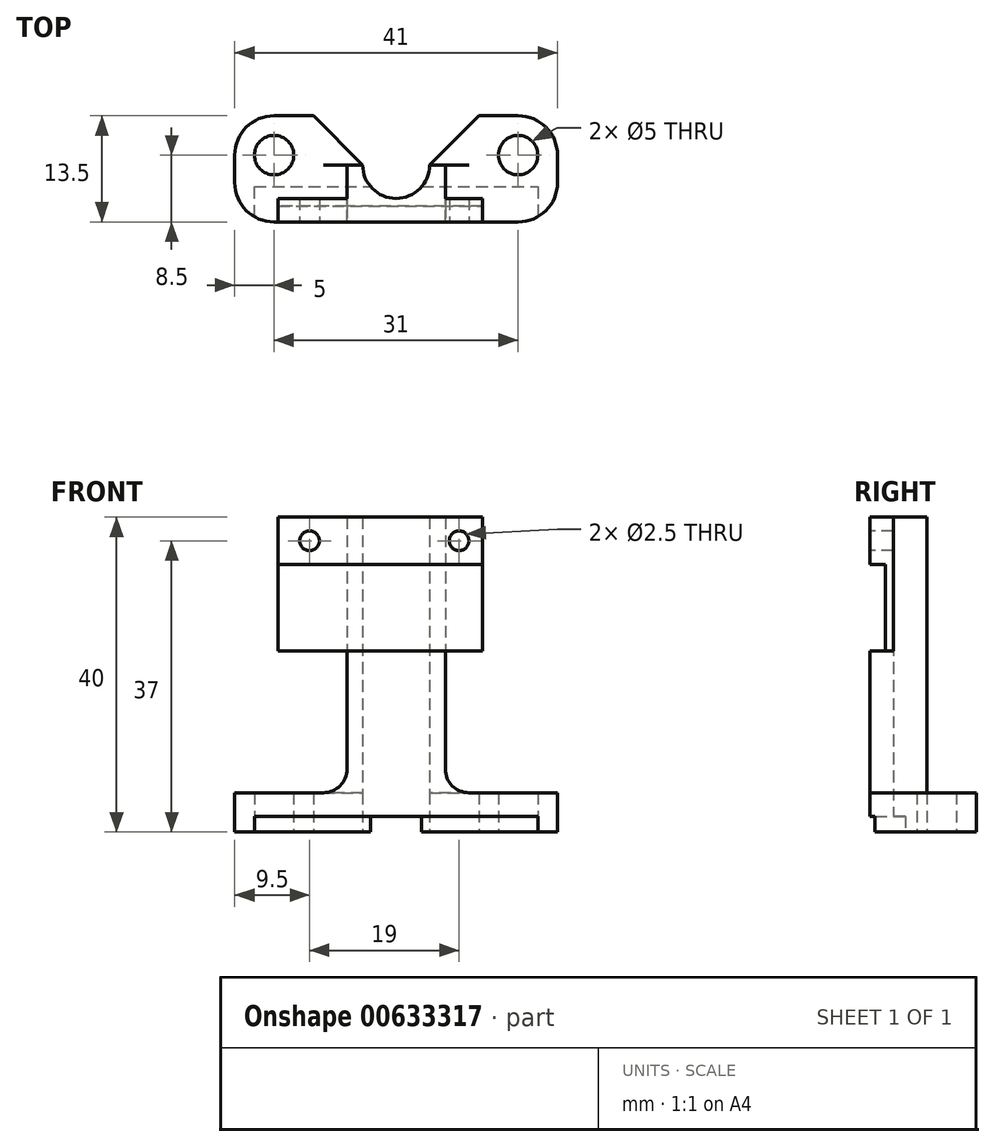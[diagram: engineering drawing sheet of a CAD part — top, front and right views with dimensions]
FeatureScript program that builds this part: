
annotation { "Feature Type Name" : "Feature", "Feature Type Description" : "" }
export const myFeature = defineFeature(function(context is Context, id is Id, definition is map)
    precondition{}
    {
        {
            var Q0;
            Q0=qCreatedBy(makeId("Top.planeOp"),FACE);
            var sketch = newSketch(context, id + "F0", { "sketchPlane" : qUnion([Q0])});
            skCircle(sketch, "E0", {"center": v(-15.5, 0) * mm, "radius": 2.5 * mm});
            skCircle(sketch, "E1", {"center": v(0, -1.25) * mm, "radius": 4.25 * mm});
            skLineSegment(sketch, "E2", {"start": v(0, -1.25) * mm, "end": v(-4.25, -1.25) * mm, "construction": true});
            skLineSegment(sketch, "E3", {"start": v(-4.25, -1.25) * mm, "end": v(-10.5, 5) * mm});
            skLineSegment(sketch, "E4", {"start": v(-10.5, 5) * mm, "end": v(-20.5, 5) * mm});
            skLineSegment(sketch, "E5", {"start": v(-20.5, 5) * mm, "end": v(-20.5, -8.5) * mm});
            skLineSegment(sketch, "E6", {"start": v(-20.5, -8.5) * mm, "end": v(0, -8.5) * mm});
            skLineSegment(sketch, "E7.MirrorCS", {"start": v(4.25, -1.25) * mm, "end": v(10.5, 5) * mm});
            skLineSegment(sketch, "E8.MirrorCS", {"start": v(20.5, -8.5) * mm, "end": v(0, -8.5) * mm});
            skLineSegment(sketch, "E9.MirrorCS", {"start": v(20.5, 5) * mm, "end": v(20.5, -8.5) * mm});
            skLineSegment(sketch, "E10.MirrorCS", {"start": v(10.5, 5) * mm, "end": v(20.5, 5) * mm});
            skCircle(sketch, "E11.MirrorC", {"center": v(15.5, 0) * mm, "radius": 2.5 * mm});
            skPoint(sketch, "E12", {"position": v(0, -5.5) * mm});
            skSolve(sketch);
        }
        {
            var Q0;
            Q0=makeQuery(id+"F0.imprint","IMPRINT",FACE,{"disambiguationData":[TD([[makeQuery(id+"F0.imprint","IMPRINT",EDGE,{"derivedFrom":sQuery(id+"F0.wireOp",EDGE,"E0")}),-1.0]])]});
            extrude(context, id + "F1", {"entities" : qUnion([Q0]), "depth" : 5 * mm, "offsetDistance" : 25 * mm});
        }
        {
            var Q0;
            Q0=makeQuery(id+"F1.opExtrude","CAP_FACE",FACE,{"disambiguationData":[OSD([sQuery(id+"F0.wireOp",EDGE,"E0"),sQuery(id+"F0.wireOp",EDGE,"E1"),sQuery(id+"F0.wireOp",EDGE,"E3"),sQuery(id+"F0.wireOp",EDGE,"E4"),sQuery(id+"F0.wireOp",EDGE,"E5"),sQuery(id+"F0.wireOp",EDGE,"E6"),sQuery(id+"F0.wireOp",EDGE,"E7.MirrorCS"),sQuery(id+"F0.wireOp",EDGE,"E8.MirrorCS"),sQuery(id+"F0.wireOp",EDGE,"E9.MirrorCS"),sQuery(id+"F0.wireOp",EDGE,"E10.MirrorCS"),sQuery(id+"F0.wireOp",EDGE,"E11.MirrorC")])],"isStart":true});
            var sketch = newSketch(context, id + "F2", { "sketchPlane" : qUnion([Q0])});
            skLineSegment(sketch, "E13", {"start": v(-4.25, 1.25) * mm, "end": v(-6.25, 1.25) * mm});
            skLineSegment(sketch, "E14", {"start": v(-6.25, 1.25) * mm, "end": v(-6.25, 8.5) * mm});
            skLineSegment(sketch, "E15.MirrorCS", {"start": v(6.25, 1.25) * mm, "end": v(6.25, 8.5) * mm});
            skLineSegment(sketch, "E16.MirrorCS", {"start": v(4.25, 1.25) * mm, "end": v(6.25, 1.25) * mm});
            skSolve(sketch);
        }
        {
            var Q0;
            Q0=makeQuery(id+"F2.imprint","IMPRINT",FACE,{"disambiguationData":[TD([[makeQuery(id+"F2.imprint","IMPRINT",EDGE,{"derivedFrom":sQuery(id+"F2.wireOp",EDGE,"E13")}),-1.0]])]});
            extrude(context, id + "F3", {"entities" : qUnion([Q0]), "operationType" : NewBodyOperationType.ADD, "oppositeDirection" : true, "depth" : 40 * mm, "offsetDistance" : 25 * mm});
        }
        {
            var Q0;
            Q0=makeQuery(id+"F3.opExtrude","CAP_FACE",FACE,{"disambiguationData":[OSD([sQuery(id+"F0.wireOp",EDGE,"E1"),sQuery(id+"F0.wireOp",EDGE,"E6"),sQuery(id+"F0.wireOp",EDGE,"E8.MirrorCS"),sQuery(id+"F2.wireOp",EDGE,"E13"),sQuery(id+"F2.wireOp",EDGE,"E14"),sQuery(id+"F2.wireOp",EDGE,"E15.MirrorCS"),sQuery(id+"F2.wireOp",EDGE,"E16.MirrorCS")])],"isStart":false});
            var sketch = newSketch(context, id + "F4", { "sketchPlane" : qUnion([Q0])});
            skLineSegment(sketch, "E17", {"start": v(-15, -5.5) * mm, "end": v(0, -5.5) * mm});
            skPoint(sketch, "E17.startSnap0", {"position": v(0, -5.5) * mm});
            skLineSegment(sketch, "E18", {"start": v(0, -5.5) * mm, "end": v(11, -5.5) * mm});
            skLineSegment(sketch, "E19", {"start": v(11, -5.5) * mm, "end": v(11, -8.5) * mm});
            skLineSegment(sketch, "E20", {"start": v(11, -8.5) * mm, "end": v(-15, -8.5) * mm});
            skLineSegment(sketch, "E21", {"start": v(-15, -8.5) * mm, "end": v(-15, -5.5) * mm});
            skSolve(sketch);
        }
        {
            var Q0;
            {var subQ0=sQuery(id+"F4.wireOp",EDGE,"E21");Q0=makeQuery(id+"F4.imprint","IMPRINT",FACE,{"disambiguationData":[TD([[makeQuery(id+"F4.imprint","IMPRINT",EDGE,{"derivedFrom":subQ0}),-1.0]])]});}
            var Q1;
            {var subQ0=sQuery(id+"F4.wireOp",EDGE,"E20");var subQ1=makeQuery(id+"F3.opExtrude","CAP_EDGE",EDGE,{"disambiguationData":[OSD([sQuery(id+"F2.wireOp",EDGE,"E14")])],"isStart":false});var subQ2=makeQuery(id+"F4.imprint","INTERSECT",VERTEX,{"derivedFrom":[subQ1,subQ0]});var subQ7=makeQuery(id+"F3.opExtrude","CAP_EDGE",EDGE,{"disambiguationData":[OSD([sQuery(id+"F2.wireOp",EDGE,"E15.MirrorCS")])],"isStart":false});var subQ9=makeQuery(id+"F4.imprint","INTERSECT",VERTEX,{"derivedFrom":[subQ7,subQ0]});Q1=makeQuery(id+"F4.imprint","IMPRINT",FACE,{"disambiguationData":[TD([[makeQuery(id+"F4.imprint","IMPRINT",EDGE,{"disambiguationData":[TD([[subQ2,-1.0],[subQ9,1.0]])],"derivedFrom":subQ0}),1.0]])]});}
            var Q2;
            {var subQ0=sQuery(id+"F4.wireOp",EDGE,"E19");Q2=makeQuery(id+"F4.imprint","IMPRINT",FACE,{"disambiguationData":[TD([[makeQuery(id+"F4.imprint","IMPRINT",EDGE,{"derivedFrom":subQ0}),-1.0]])]});}
            extrude(context, id + "F5", {"entities" : qUnion([Q0, Q1, Q2]), "operationType" : NewBodyOperationType.ADD, "oppositeDirection" : true, "depth" : 17 * mm, "offsetDistance" : 25 * mm});
        }
        {
            var Q0;
            {var subQ0=sQuery(id+"F0.wireOp",EDGE,"E8.MirrorCS");var subQ1=sQuery(id+"F0.wireOp",EDGE,"E6");Q0=makeQuery(id+"F5.boolean.opBoolean","MERGE",FACE,{"derivedFrom":[makeQuery(id+"F3.boolean.opBoolean","MERGE",FACE,{"derivedFrom":[makeQuery(id+"F1.opExtrude","SWEPT_FACE",FACE,{"disambiguationData":[OSD([subQ1,subQ0])]}),makeQuery(id+"F3.opExtrude","SWEPT_FACE",FACE,{"disambiguationData":[OSD([subQ1,subQ0])]})]}),makeQuery(id+"F5.opExtrude","SWEPT_FACE",FACE,{"disambiguationData":[OSD([sQuery(id+"F4.wireOp",EDGE,"E20")])]})]});}
            var sketch = newSketch(context, id + "F6", { "sketchPlane" : qUnion([Q0])});
            skPoint(sketch, "E22", {"position": v(-11, 37) * mm});
            skPoint(sketch, "E23", {"position": v(8, 37) * mm});
            skLineSegment(sketch, "E24", {"start": v(-15, 34) * mm, "end": v(11, 34) * mm});
            skLineSegment(sketch, "E25", {"start": v(-6.25, 23) * mm, "end": v(6.25, 23) * mm});
            skSolve(sketch);
        }
        {
            var Q0;
            {var subQ11=sQuery(id+"F6.wireOp",EDGE,"E24");Q0=makeQuery(id+"F6.imprint","IMPRINT",FACE,{"disambiguationData":[TD([[makeQuery(id+"F6.imprint","IMPRINT",EDGE,{"derivedFrom":subQ11}),-1.0]])]});}
            extrude(context, id + "F7", {"entities" : qUnion([Q0]), "operationType" : NewBodyOperationType.REMOVE, "oppositeDirection" : true, "depth" : 2 * mm, "offsetDistance" : 25 * mm});
        }
        {
            var Q0;
            Q0=sQuery(id+"F6.wireOp",VERTEX,"E22");
            var Q1;
            Q1=sQuery(id+"F6.wireOp",VERTEX,"E23");
            var Q2;
            Q2=makeQuery(id+"F1.opExtrude","SWEPT_BODY",BODY,{"disambiguationData":[OSD([sQuery(id+"F0.wireOp",EDGE,"E0"),sQuery(id+"F0.wireOp",EDGE,"E1"),sQuery(id+"F0.wireOp",EDGE,"E3"),sQuery(id+"F0.wireOp",EDGE,"E4"),sQuery(id+"F0.wireOp",EDGE,"E5"),sQuery(id+"F0.wireOp",EDGE,"E6"),sQuery(id+"F0.wireOp",EDGE,"E7.MirrorCS"),sQuery(id+"F0.wireOp",EDGE,"E8.MirrorCS"),sQuery(id+"F0.wireOp",EDGE,"E9.MirrorCS"),sQuery(id+"F0.wireOp",EDGE,"E10.MirrorCS"),sQuery(id+"F0.wireOp",EDGE,"E11.MirrorC")])]});
            hole(context, id + "F8", {"style" : HoleStyle.SIMPLE, "endStyle" : HoleEndStyle.THROUGH, "holeDiameter" : 2.5 * mm, "majorDiameter" : 5 * mm, "tappedDepth" : 12 * mm, "tapClearance" : 3, "locations" : qUnion([Q0, Q1]), "scope" : qUnion([Q2])});
        }
        {
            var Q0;
            Q0=makeQuery(id+"F1.opExtrude","SWEPT_EDGE",EDGE,{"disambiguationData":[OSD([sQuery(id+"F0.wireOp",EDGE,"E8.MirrorCS"),sQuery(id+"F0.wireOp",EDGE,"E9.MirrorCS")])]});
            var Q1;
            Q1=makeQuery(id+"F1.opExtrude","SWEPT_EDGE",EDGE,{"disambiguationData":[OSD([sQuery(id+"F0.wireOp",EDGE,"E4"),sQuery(id+"F0.wireOp",EDGE,"E5")])]});
            var Q2;
            Q2=makeQuery(id+"F1.opExtrude","SWEPT_EDGE",EDGE,{"disambiguationData":[OSD([sQuery(id+"F0.wireOp",EDGE,"E5"),sQuery(id+"F0.wireOp",EDGE,"E6")])]});
            var Q3;
            Q3=makeQuery(id+"F1.opExtrude","SWEPT_EDGE",EDGE,{"disambiguationData":[OSD([sQuery(id+"F0.wireOp",EDGE,"E9.MirrorCS"),sQuery(id+"F0.wireOp",EDGE,"E10.MirrorCS")])]});
            fillet(context, id + "F9", {"entities" : qUnion([Q0, Q1, Q2, Q3]), "radius" : 5 * mm, "tangentPropagation" : true, "allowEdgeOverflow" : false});
        }
        {
            var Q0;
            Q0=makeQuery(id+"F1.opExtrude","CAP_FACE",FACE,{"disambiguationData":[OSD([sQuery(id+"F0.wireOp",EDGE,"E0"),sQuery(id+"F0.wireOp",EDGE,"E1"),sQuery(id+"F0.wireOp",EDGE,"E3"),sQuery(id+"F0.wireOp",EDGE,"E4"),sQuery(id+"F0.wireOp",EDGE,"E5"),sQuery(id+"F0.wireOp",EDGE,"E6"),sQuery(id+"F0.wireOp",EDGE,"E7.MirrorCS"),sQuery(id+"F0.wireOp",EDGE,"E8.MirrorCS"),sQuery(id+"F0.wireOp",EDGE,"E9.MirrorCS"),sQuery(id+"F0.wireOp",EDGE,"E10.MirrorCS"),sQuery(id+"F0.wireOp",EDGE,"E11.MirrorC")])],"isStart":true});
            var sketch = newSketch(context, id + "F10", { "sketchPlane" : qUnion([Q0])});
            skPoint(sketch, "E26", {"position": v(-18, 0) * mm});
            skPoint(sketch, "E27", {"position": v(18, 0) * mm});
            skPoint(sketch, "E28", {"position": v(15.5, 0) * mm});
            skPoint(sketch, "E29", {"position": v(-15.5, 0) * mm});
            skPoint(sketch, "E30", {"position": v(-15.5, 2.5) * mm});
            skPoint(sketch, "E31", {"position": v(15.5, 2.5) * mm});
            skLineSegment(sketch, "E32", {"start": v(-18, 7.83) * mm, "end": v(-18, 4) * mm});
            skLineSegment(sketch, "E33", {"start": v(-18, 4) * mm, "end": v(-3.24, 4) * mm});
            skLineSegment(sketch, "E34", {"start": v(18, 4) * mm, "end": v(18, 7.83) * mm});
            skArc(sketch, "E35.0", {"start": v(-3.24, 4) * mm, "mid": v(0, 5.5) * mm, "end": v(3.24, 4) * mm});
            skLineSegment(sketch, "E36.trimOffspring", {"start": v(3.24, 4) * mm, "end": v(18, 4) * mm});
            skPoint(sketch, "E37.orphan", {"position": v(-4.25, 1.25) * mm});
            skPoint(sketch, "E38.orphan", {"position": v(4.25, 1.25) * mm});
            skSolve(sketch);
        }
        {
            var Q0;
            {var subQ4=sQuery(id+"F10.wireOp",EDGE,"E32");Q0=makeQuery(id+"F10.imprint","IMPRINT",FACE,{"disambiguationData":[TD([[makeQuery(id+"F10.imprint","IMPRINT",EDGE,{"derivedFrom":subQ4}),1.0]])]});}
            extrude(context, id + "F11", {"entities" : qUnion([Q0]), "operationType" : NewBodyOperationType.REMOVE, "oppositeDirection" : true, "depth" : 2 * mm, "offsetDistance" : 25 * mm});
        }
        {
            var Q0;
            Q0=makeQuery(id+"F3.boolean.opBoolean","INTERSECT",EDGE,{"derivedFrom":[makeQuery(id+"F1.opExtrude","CAP_FACE",FACE,{"disambiguationData":[OSD([sQuery(id+"F0.wireOp",EDGE,"E0"),sQuery(id+"F0.wireOp",EDGE,"E1"),sQuery(id+"F0.wireOp",EDGE,"E3"),sQuery(id+"F0.wireOp",EDGE,"E4"),sQuery(id+"F0.wireOp",EDGE,"E5"),sQuery(id+"F0.wireOp",EDGE,"E6"),sQuery(id+"F0.wireOp",EDGE,"E7.MirrorCS"),sQuery(id+"F0.wireOp",EDGE,"E8.MirrorCS"),sQuery(id+"F0.wireOp",EDGE,"E9.MirrorCS"),sQuery(id+"F0.wireOp",EDGE,"E10.MirrorCS"),sQuery(id+"F0.wireOp",EDGE,"E11.MirrorC")])],"isStart":false}),makeQuery(id+"F3.opExtrude","SWEPT_FACE",FACE,{"disambiguationData":[OSD([sQuery(id+"F2.wireOp",EDGE,"E15.MirrorCS")])]})]});
            var Q1;
            Q1=makeQuery(id+"F3.boolean.opBoolean","INTERSECT",EDGE,{"derivedFrom":[makeQuery(id+"F1.opExtrude","CAP_FACE",FACE,{"disambiguationData":[OSD([sQuery(id+"F0.wireOp",EDGE,"E0"),sQuery(id+"F0.wireOp",EDGE,"E1"),sQuery(id+"F0.wireOp",EDGE,"E3"),sQuery(id+"F0.wireOp",EDGE,"E4"),sQuery(id+"F0.wireOp",EDGE,"E5"),sQuery(id+"F0.wireOp",EDGE,"E6"),sQuery(id+"F0.wireOp",EDGE,"E7.MirrorCS"),sQuery(id+"F0.wireOp",EDGE,"E8.MirrorCS"),sQuery(id+"F0.wireOp",EDGE,"E9.MirrorCS"),sQuery(id+"F0.wireOp",EDGE,"E10.MirrorCS"),sQuery(id+"F0.wireOp",EDGE,"E11.MirrorC")])],"isStart":false}),makeQuery(id+"F3.opExtrude","SWEPT_FACE",FACE,{"disambiguationData":[OSD([sQuery(id+"F2.wireOp",EDGE,"E14")])]})]});
            fillet(context, id + "F12", {"entities" : qUnion([Q0, Q1]), "radius" : 3 * mm, "tangentPropagation" : true, "allowEdgeOverflow" : false});
        }
    });
